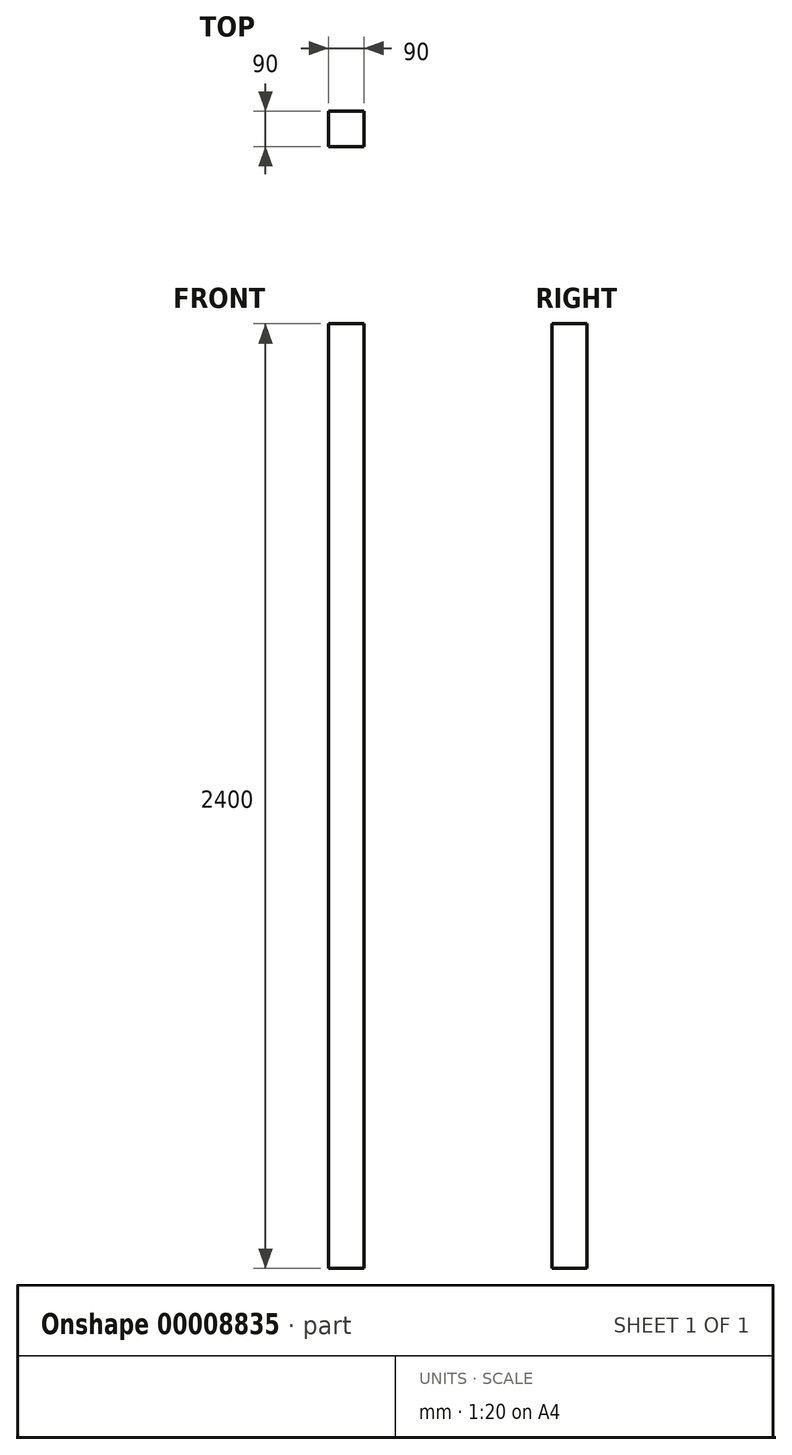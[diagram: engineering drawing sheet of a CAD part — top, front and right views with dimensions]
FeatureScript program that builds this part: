
annotation { "Feature Type Name" : "Feature", "Feature Type Description" : "" }
export const myFeature = defineFeature(function(context is Context, id is Id, definition is map)
    precondition{}
    {
        {
            var Q0;
            Q0=qCreatedBy(makeId("Top.planeOp"),FACE);
            var sketch = newSketch(context, id + "F0", { "sketchPlane" : qUnion([Q0])});
            skLineSegment(sketch, "E0.bottom", {"start": v(0, 0) * mm, "end": v(90, 0) * mm});
            skLineSegment(sketch, "E0.top", {"start": v(0, 90) * mm, "end": v(90, 90) * mm});
            skLineSegment(sketch, "E0.left", {"start": v(0, 0) * mm, "end": v(0, 90) * mm});
            skLineSegment(sketch, "E0.right", {"start": v(90, 0) * mm, "end": v(90, 90) * mm});
            skSolve(sketch);
        }
        {
            var Q0;
            Q0=makeQuery(id+"F0.imprint","IMPRINT",FACE,{"disambiguationData":[TD([[makeQuery(id+"F0.imprint","IMPRINT",EDGE,{"derivedFrom":sQuery(id+"F0.wireOp",EDGE,"E0.bottom")}),1.0]])]});
            extrude(context, id + "F1", {"entities" : qUnion([Q0]), "depth" : 2400 * mm});
        }
    });
